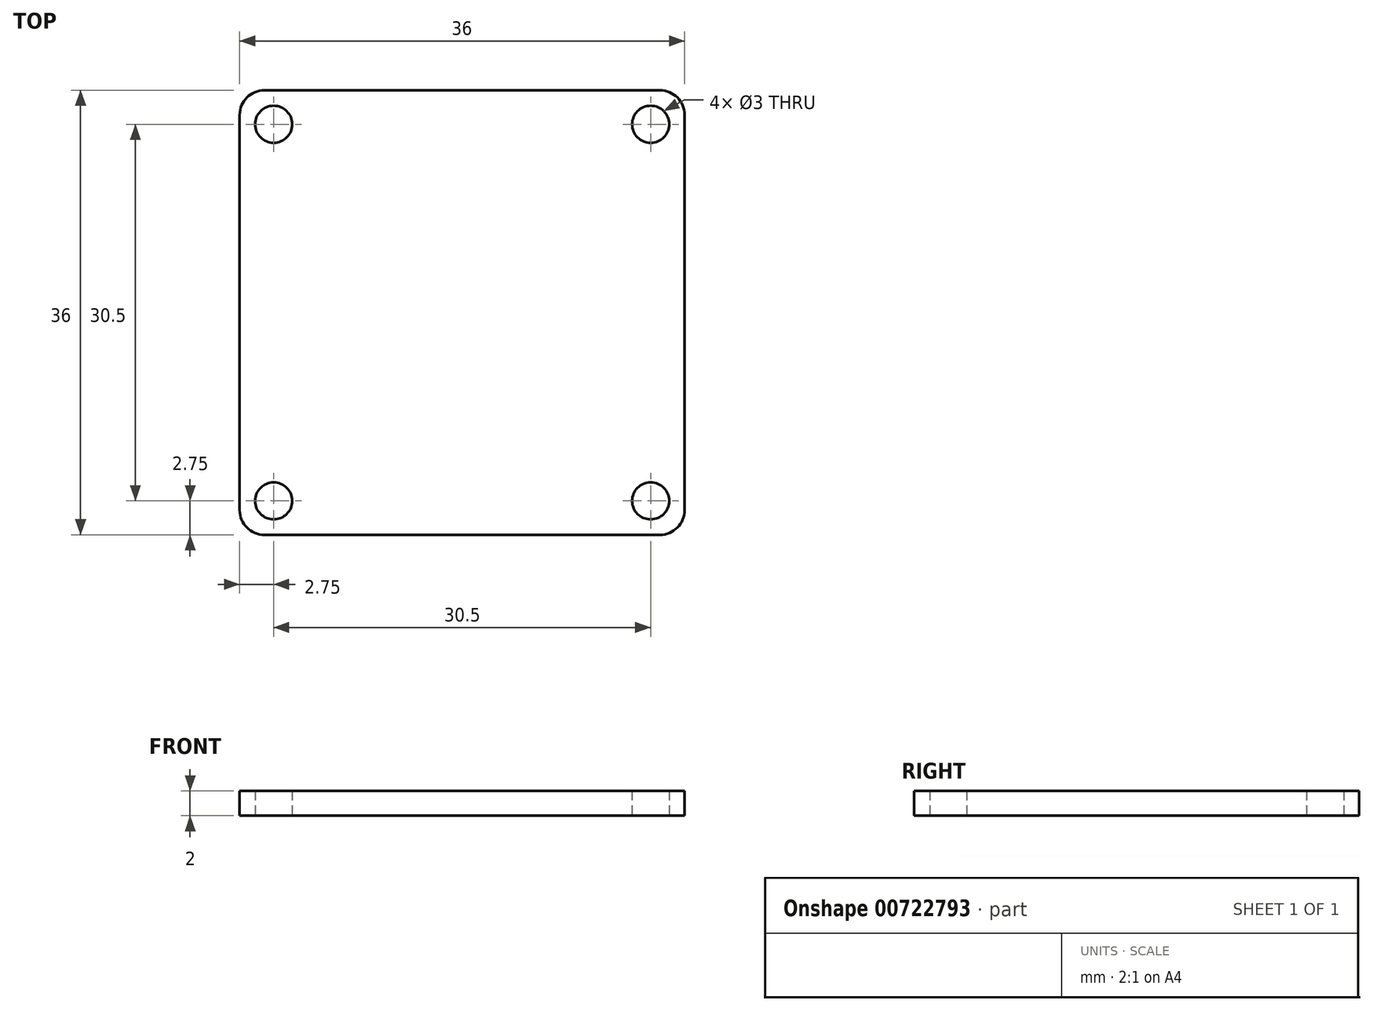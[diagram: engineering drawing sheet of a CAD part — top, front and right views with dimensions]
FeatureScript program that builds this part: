
annotation { "Feature Type Name" : "Feature", "Feature Type Description" : "" }
export const myFeature = defineFeature(function(context is Context, id is Id, definition is map)
    precondition{}
    {
        {
            var Q0;
            Q0=qCreatedBy(makeId("Top.planeOp"),FACE);
            var sketch = newSketch(context, id + "F0", { "sketchPlane" : qUnion([Q0])});
            skLineSegment(sketch, "E0.bottom", {"start": v(15.25, -15.25) * mm, "end": v(-15.25, -15.25) * mm, "construction": true});
            skLineSegment(sketch, "E0.top", {"start": v(15.25, 15.25) * mm, "end": v(-15.25, 15.25) * mm, "construction": true});
            skLineSegment(sketch, "E0.left", {"start": v(15.25, -15.25) * mm, "end": v(15.25, 15.25) * mm, "construction": true});
            skLineSegment(sketch, "E0.right", {"start": v(-15.25, -15.25) * mm, "end": v(-15.25, 15.25) * mm, "construction": true});
            skPoint(sketch, "E0.middle", {"position": v(0, 0) * mm});
            skCircle(sketch, "E1", {"center": v(-15.25, 15.25) * mm, "radius": 1.5 * mm});
            skCircle(sketch, "E2", {"center": v(-15.25, -15.25) * mm, "radius": 1.5 * mm});
            skCircle(sketch, "E3", {"center": v(15.25, -15.25) * mm, "radius": 1.5 * mm});
            skCircle(sketch, "E4", {"center": v(15.25, 15.25) * mm, "radius": 1.5 * mm});
            skLineSegment(sketch, "E5.bottom", {"start": v(16, 18) * mm, "end": v(-16, 18) * mm});
            skLineSegment(sketch, "E5.top", {"start": v(16, -18) * mm, "end": v(-16, -18) * mm});
            skLineSegment(sketch, "E5.left", {"start": v(18, 16) * mm, "end": v(18, -16) * mm});
            skLineSegment(sketch, "E5.right", {"start": v(-18, 16) * mm, "end": v(-18, -16) * mm});
            skPoint(sketch, "E6.visualSharp", {"position": v(-18, 18) * mm});
            skArc(sketch, "E6.filletArc", {"start": v(-16, 18) * mm, "mid": v(-17.41, 17.41) * mm, "end": v(-18, 16) * mm});
            skPoint(sketch, "E7.visualSharp", {"position": v(18, 18) * mm});
            skArc(sketch, "E7.filletArc", {"start": v(18, 16) * mm, "mid": v(17.41, 17.41) * mm, "end": v(16, 18) * mm});
            skPoint(sketch, "E8.visualSharp", {"position": v(18, -18) * mm});
            skArc(sketch, "E8.filletArc", {"start": v(16, -18) * mm, "mid": v(17.41, -17.41) * mm, "end": v(18, -16) * mm});
            skPoint(sketch, "E9.visualSharp", {"position": v(-18, -18) * mm});
            skArc(sketch, "E9.filletArc", {"start": v(-18, -16) * mm, "mid": v(-17.41, -17.41) * mm, "end": v(-16, -18) * mm});
            skSolve(sketch);
        }
        {
            var Q0;
            Q0 = qSketchRegion(id + "F0", true);
            extrude(context, id + "F1", {"entities" : qUnion([Q0]), "depth" : 2 * mm, "offsetDistance" : 25 * mm});
        }
    });
